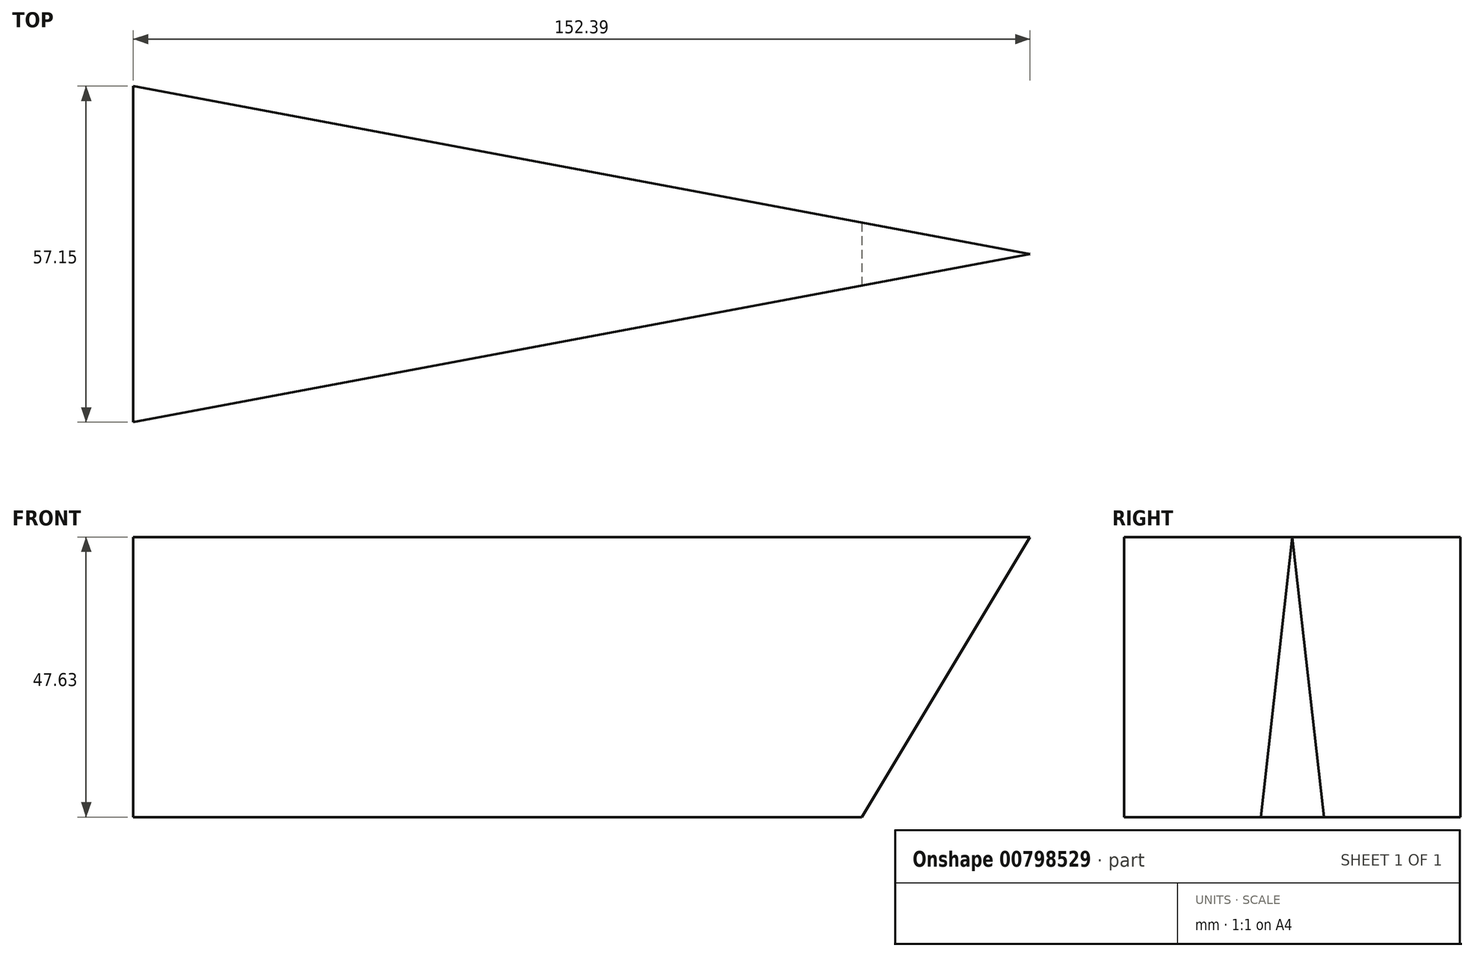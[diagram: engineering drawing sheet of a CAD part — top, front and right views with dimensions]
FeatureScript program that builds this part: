
annotation { "Feature Type Name" : "Feature", "Feature Type Description" : "" }
export const myFeature = defineFeature(function(context is Context, id is Id, definition is map)
    precondition{}
    {
        {
            var Q0;
            Q0=qCreatedBy(makeId("Front.planeOp"),FACE);
            var sketch = newSketch(context, id + "F0", { "sketchPlane" : qUnion([Q0])});
            skLineSegment(sketch, "E0", {"start": v(0, 0) * mm, "end": v(152.4, 0) * mm});
            skLineSegment(sketch, "E1", {"start": v(152.4, 0) * mm, "end": v(152.4, 47.63) * mm});
            skLineSegment(sketch, "E2", {"start": v(152.4, 47.63) * mm, "end": v(0, 47.63) * mm});
            skLineSegment(sketch, "E3", {"start": v(0, 47.63) * mm, "end": v(0, 0) * mm});
            skSolve(sketch);
        }
        {
            var Q0;
            Q0=makeQuery(id+"F0.imprint","IMPRINT",FACE,{"disambiguationData":[TD([[makeQuery(id+"F0.imprint","IMPRINT",EDGE,{"derivedFrom":sQuery(id+"F0.wireOp",EDGE,"E0")}),1.0]])]});
            extrude(context, id + "F1", {"entities" : qUnion([Q0]), "depth" : 57.15 * mm, "offsetDistance" : 25.4 * mm});
        }
        {
            var Q0;
            Q0=makeQuery(id+"F1.opExtrude","CAP_FACE",FACE,{"disambiguationData":[OSD([sQuery(id+"F0.wireOp",EDGE,"E0"),sQuery(id+"F0.wireOp",EDGE,"E1"),sQuery(id+"F0.wireOp",EDGE,"E2"),sQuery(id+"F0.wireOp",EDGE,"E3")])],"isStart":false});
            var sketch = newSketch(context, id + "F2", { "sketchPlane" : qUnion([Q0])});
            skLineSegment(sketch, "E4", {"start": v(152.4, 47.62) * mm, "end": v(123.82, 0) * mm});
            skLineSegment(sketch, "E5", {"start": v(123.82, 0) * mm, "end": v(152.4, 0) * mm});
            skLineSegment(sketch, "E6", {"start": v(152.4, 0) * mm, "end": v(152.4, 47.63) * mm});
            skSolve(sketch);
        }
        {
            var Q0;
            Q0=makeQuery(id+"F2.imprint","IMPRINT",FACE,{"disambiguationData":[TD([[makeQuery(id+"F2.imprint","IMPRINT",EDGE,{"derivedFrom":sQuery(id+"F2.wireOp",EDGE,"E4")}),1.0]])]});
            extrude(context, id + "F3", {"entities" : qUnion([Q0]), "operationType" : NewBodyOperationType.REMOVE, "oppositeDirection" : true, "depth" : 57.15 * mm, "offsetDistance" : 25.4 * mm});
        }
        {
            var Q0;
            Q0=makeQuery(id+"F1.opExtrude","SWEPT_FACE",FACE,{"disambiguationData":[OSD([sQuery(id+"F0.wireOp",EDGE,"E2")])]});
            var sketch = newSketch(context, id + "F4", { "sketchPlane" : qUnion([Q0])});
            skLineSegment(sketch, "E7", {"start": v(152.4, -28.58) * mm, "end": v(0, 0) * mm});
            skLineSegment(sketch, "E8", {"start": v(0, 0) * mm, "end": v(152.4, 0) * mm});
            skLineSegment(sketch, "E9", {"start": v(152.4, 0) * mm, "end": v(152.4, -28.58) * mm});
            skSolve(sketch);
        }
        {
            var Q0;
            Q0=makeQuery(id+"F4.imprint","IMPRINT",FACE,{"disambiguationData":[TD([[makeQuery(id+"F4.imprint","IMPRINT",EDGE,{"derivedFrom":sQuery(id+"F4.wireOp",EDGE,"E7")}),-1.0]])]});
            extrude(context, id + "F5", {"entities" : qUnion([Q0]), "operationType" : NewBodyOperationType.ADD, "depth" : 76.2 * mm, "offsetDistance" : 25.4 * mm});
        }
        {
            var Q0;
            Q0=makeQuery(id+"F5.opExtrude","CAP_FACE",FACE,{"disambiguationData":[OSD([sQuery(id+"F4.wireOp",EDGE,"E7"),sQuery(id+"F4.wireOp",EDGE,"E8"),sQuery(id+"F4.wireOp",EDGE,"E9")])],"isStart":false});
            extrude(context, id + "F6", {"entities" : qUnion([Q0]), "operationType" : NewBodyOperationType.REMOVE, "oppositeDirection" : true, "depth" : 127 * mm, "offsetDistance" : 25.4 * mm});
        }
        {
            var Q0;
            Q0=makeQuery(id+"F1.opExtrude","SWEPT_FACE",FACE,{"disambiguationData":[OSD([sQuery(id+"F0.wireOp",EDGE,"E2")])]});
            var sketch = newSketch(context, id + "F7", { "sketchPlane" : qUnion([Q0])});
            skLineSegment(sketch, "E10", {"start": v(152.4, -28.58) * mm, "end": v(0, -57.15) * mm});
            skLineSegment(sketch, "E11", {"start": v(0, -57.15) * mm, "end": v(152.4, -57.15) * mm});
            skLineSegment(sketch, "E12", {"start": v(152.4, -57.15) * mm, "end": v(152.4, -28.58) * mm});
            skSolve(sketch);
        }
        {
            var Q0;
            Q0=makeQuery(id+"F7.imprint","IMPRINT",FACE,{"disambiguationData":[TD([[makeQuery(id+"F7.imprint","IMPRINT",EDGE,{"derivedFrom":sQuery(id+"F7.wireOp",EDGE,"E10")}),1.0]])]});
            extrude(context, id + "F8", {"entities" : qUnion([Q0]), "operationType" : NewBodyOperationType.REMOVE, "oppositeDirection" : true, "depth" : 50.8 * mm, "offsetDistance" : 25.4 * mm});
        }
    });
